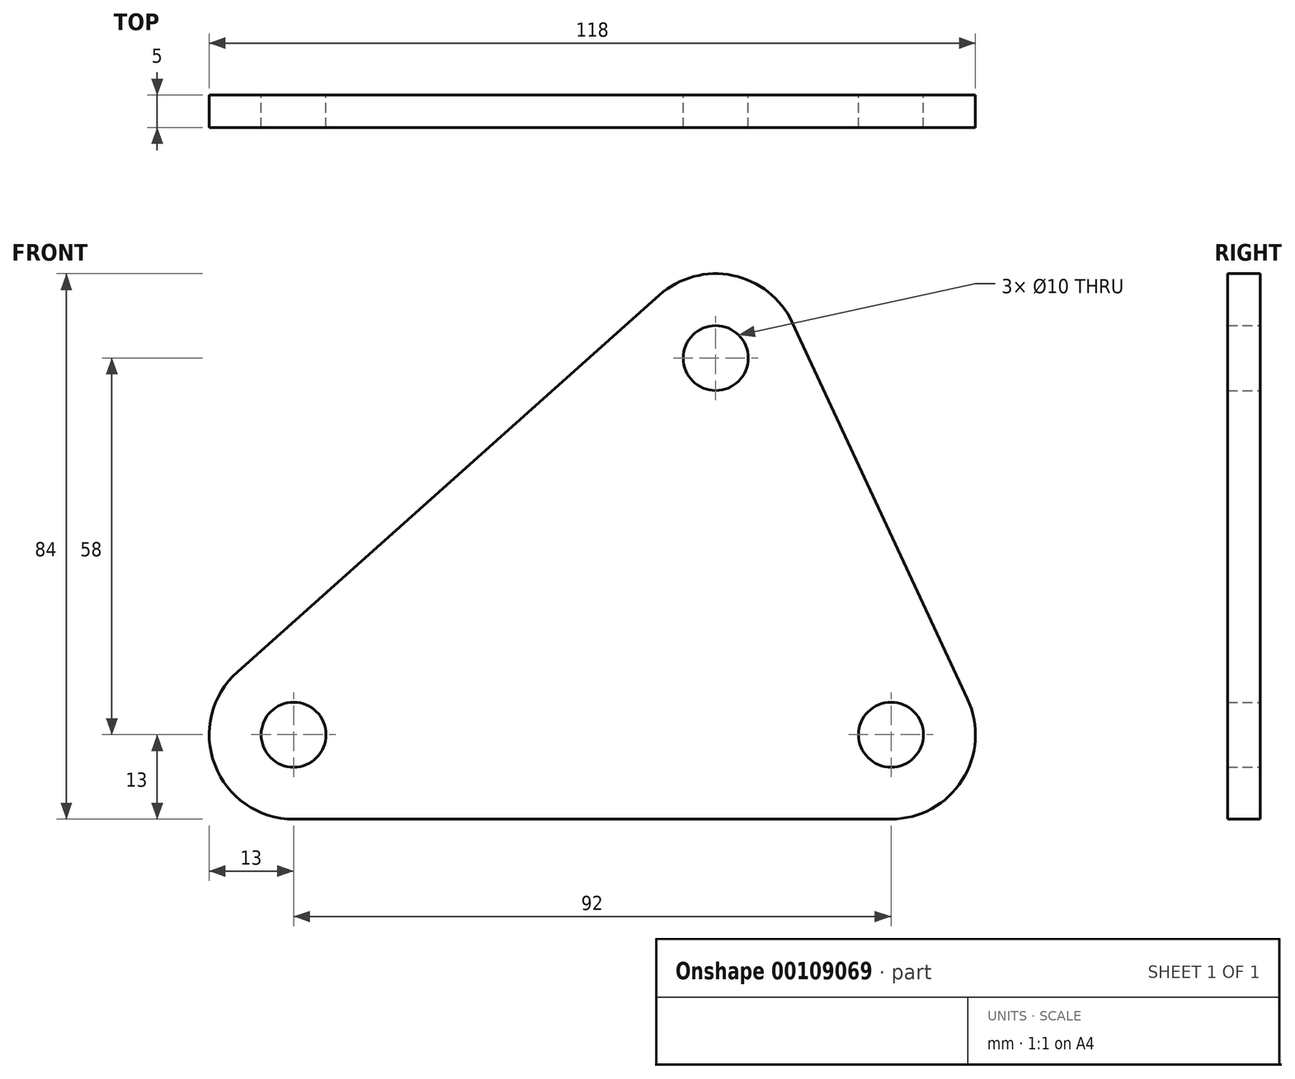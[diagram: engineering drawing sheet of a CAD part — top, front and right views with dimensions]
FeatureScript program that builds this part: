
annotation { "Feature Type Name" : "Feature", "Feature Type Description" : "" }
export const myFeature = defineFeature(function(context is Context, id is Id, definition is map)
    precondition{}
    {
        {
            var Q0;
            Q0=qCreatedBy(makeId("Front.planeOp"),FACE);
            var sketch = newSketch(context, id + "F0", { "sketchPlane" : qUnion([Q0])});
            skLineSegment(sketch, "E0", {"start": v(0, 0) * mm, "end": v(130, 0) * mm, "construction": true});
            skCircle(sketch, "E1", {"center": v(15, 25) * mm, "radius": 5 * mm});
            skCircle(sketch, "E2", {"center": v(107, 25) * mm, "radius": 5 * mm});
            skCircle(sketch, "E3", {"center": v(80, 83) * mm, "radius": 5 * mm});
            skCircle(sketch, "E4.0", {"center": v(80, 83) * mm, "radius": 13 * mm});
            skCircle(sketch, "E5.0", {"center": v(107, 25) * mm, "radius": 13 * mm});
            skCircle(sketch, "E6.0", {"center": v(15, 25) * mm, "radius": 13 * mm});
            skLineSegment(sketch, "E7", {"start": v(71.34, 92.7) * mm, "end": v(6.34, 34.7) * mm});
            skLineSegment(sketch, "E8", {"start": v(15, 12) * mm, "end": v(107, 12) * mm});
            skLineSegment(sketch, "E9", {"start": v(91.79, 88.49) * mm, "end": v(118.79, 30.49) * mm});
            skSolve(sketch);
        }
        {
            var Q0;
            {var subQ0=sQuery(id+"F0.wireOp",EDGE,"E7");Q0=makeQuery(id+"F0.imprint","IMPRINT",FACE,{"disambiguationData":[TD([[makeQuery(id+"F0.imprint","IMPRINT",EDGE,{"derivedFrom":subQ0}),1.0]])]});}
            var Q1;
            Q1=makeQuery(id+"F0.imprint","IMPRINT",FACE,{"disambiguationData":[TD([[makeQuery(id+"F0.imprint","IMPRINT",EDGE,{"derivedFrom":sQuery(id+"F0.wireOp",EDGE,"E1")}),-1.0]])]});
            var Q2;
            Q2=makeQuery(id+"F0.imprint","IMPRINT",FACE,{"disambiguationData":[TD([[makeQuery(id+"F0.imprint","IMPRINT",EDGE,{"derivedFrom":sQuery(id+"F0.wireOp",EDGE,"E3")}),-1.0]])]});
            var Q3;
            Q3=makeQuery(id+"F0.imprint","IMPRINT",FACE,{"disambiguationData":[TD([[makeQuery(id+"F0.imprint","IMPRINT",EDGE,{"derivedFrom":sQuery(id+"F0.wireOp",EDGE,"E2")}),-1.0]])]});
            extrude(context, id + "F1", {"entities" : qUnion([Q0, Q1, Q2, Q3]), "depth" : 5 * mm});
        }
    });
